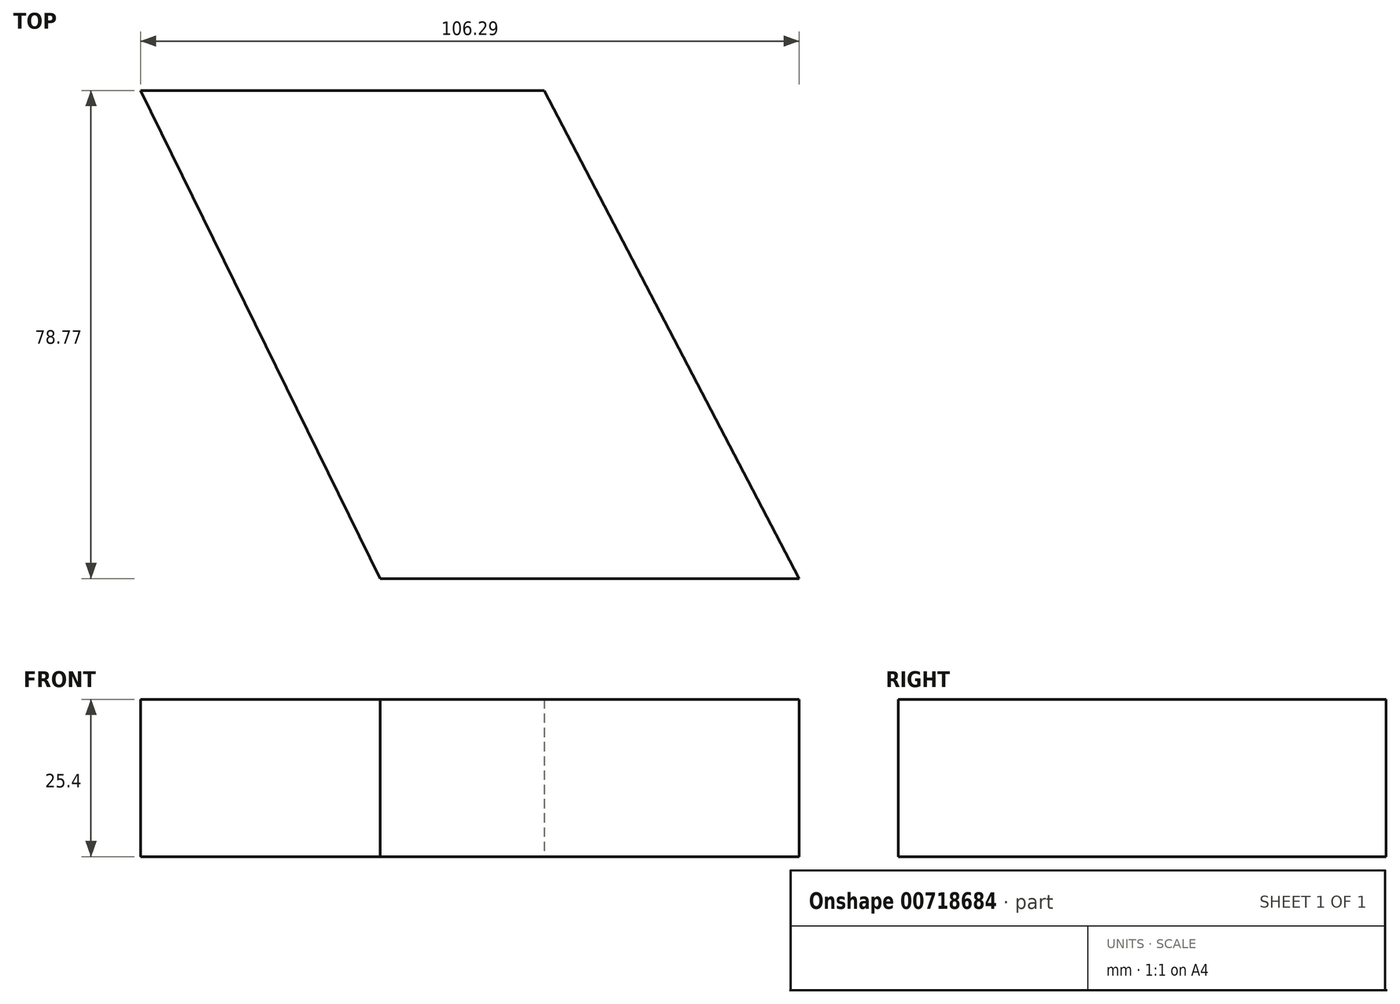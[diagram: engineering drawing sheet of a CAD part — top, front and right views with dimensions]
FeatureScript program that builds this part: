
annotation { "Feature Type Name" : "Feature", "Feature Type Description" : "" }
export const myFeature = defineFeature(function(context is Context, id is Id, definition is map)
    precondition{}
    {
        {
            var Q0;
            Q0=qCreatedBy(makeId("Top.planeOp"),FACE);
            var sketch = newSketch(context, id + "F0", { "sketchPlane" : qUnion([Q0])});
            skLineSegment(sketch, "E0", {"start": v(-106.3, 78.77) * mm, "end": v(-41.17, 78.77) * mm});
            skLineSegment(sketch, "E1", {"start": v(-41.17, 78.77) * mm, "end": v(0, 0) * mm});
            skLineSegment(sketch, "E2", {"start": v(0, 0) * mm, "end": v(-67.6, 0) * mm});
            skLineSegment(sketch, "E3", {"start": v(-67.6, 0) * mm, "end": v(-106.3, 78.77) * mm});
            skSolve(sketch);
        }
        {
            var Q0;
            Q0 = qSketchRegion(id + "F0", true);
            extrude(context, id + "F1", {"entities" : qUnion([Q0]), "depth" : 25.4 * mm, "offsetDistance" : 25.4 * mm});
        }
    });
